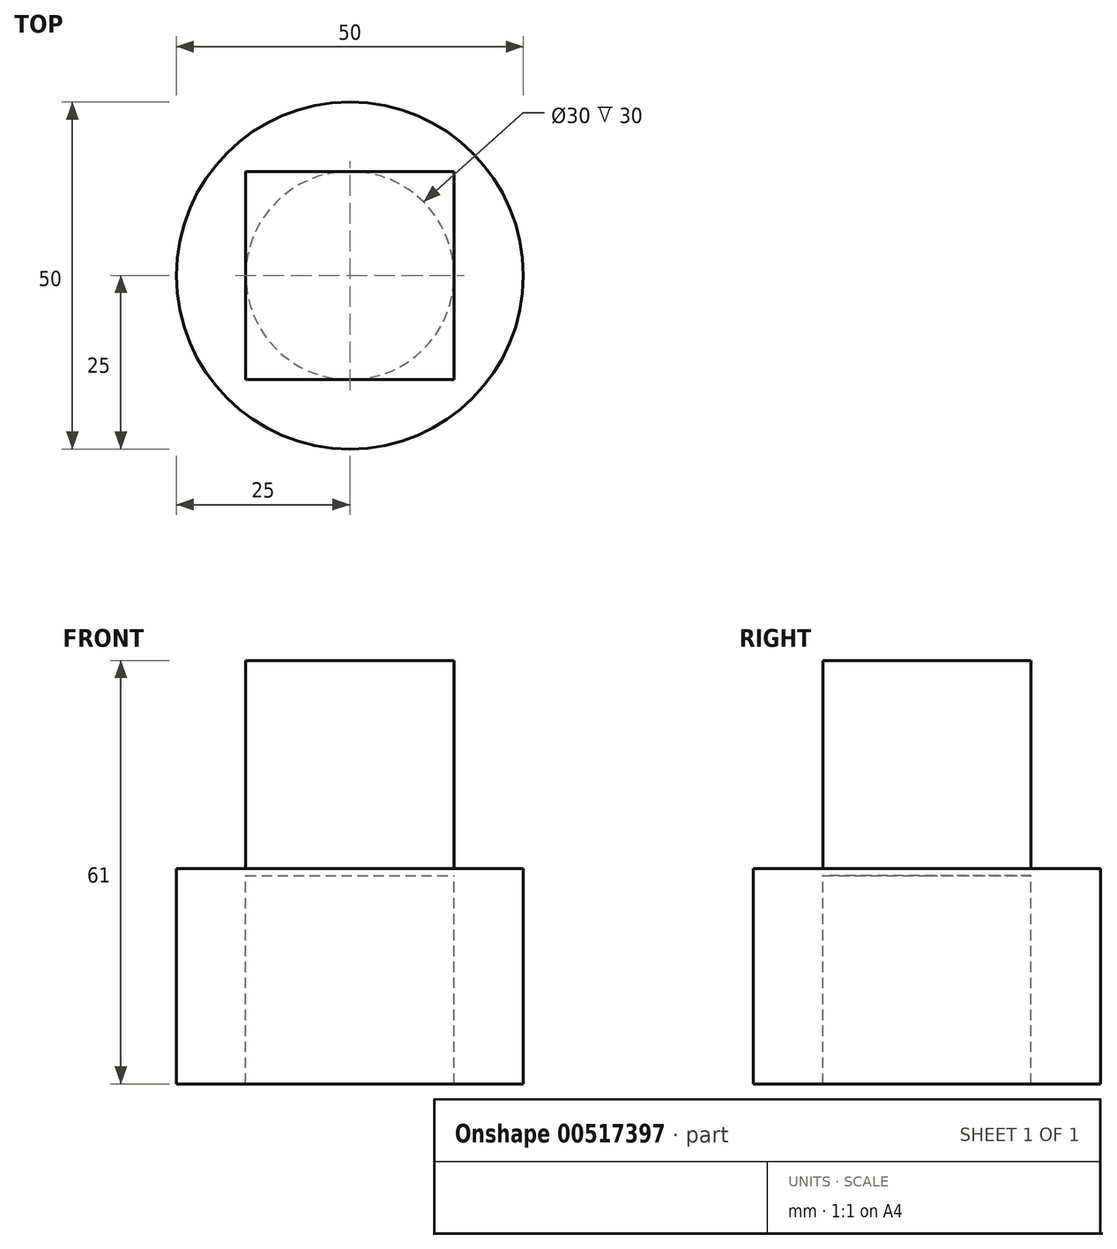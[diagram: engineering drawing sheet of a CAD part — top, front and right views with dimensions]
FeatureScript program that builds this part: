
annotation { "Feature Type Name" : "Feature", "Feature Type Description" : "" }
export const myFeature = defineFeature(function(context is Context, id is Id, definition is map)
    precondition{}
    {
        {
            var Q0;
            Q0=qCreatedBy(makeId("Top.planeOp"),FACE);
            var sketch = newSketch(context, id + "F0", { "sketchPlane" : qUnion([Q0])});
            skLineSegment(sketch, "E0.bottom", {"start": v(15, 15) * mm, "end": v(-15, 15) * mm});
            skLineSegment(sketch, "E0.top", {"start": v(15, -15) * mm, "end": v(-15, -15) * mm});
            skLineSegment(sketch, "E0.left", {"start": v(15, 15) * mm, "end": v(15, -15) * mm});
            skLineSegment(sketch, "E0.right", {"start": v(-15, 15) * mm, "end": v(-15, -15) * mm});
            skPoint(sketch, "E0.middle", {"position": v(0, 0) * mm});
            skSolve(sketch);
        }
        {
            var Q0;
            Q0=makeQuery(id+"F0.imprint","IMPRINT",FACE,{"disambiguationData":[TD([[makeQuery(id+"F0.imprint","IMPRINT",EDGE,{"derivedFrom":sQuery(id+"F0.wireOp",EDGE,"E0.bottom")}),1.0]])]});
            extrude(context, id + "F1", {"entities" : qUnion([Q0]), "depth" : 30 * mm, "offsetDistance" : 25 * mm});
        }
        {
            var Q0;
            Q0=makeQuery(id+"F1.opExtrude","CAP_FACE",FACE,{"disambiguationData":[OSD([sQuery(id+"F0.wireOp",EDGE,"E0.bottom"),sQuery(id+"F0.wireOp",EDGE,"E0.top"),sQuery(id+"F0.wireOp",EDGE,"E0.left"),sQuery(id+"F0.wireOp",EDGE,"E0.right")])],"isStart":true});
            var sketch = newSketch(context, id + "F2", { "sketchPlane" : qUnion([Q0])});
            skCircle(sketch, "E1", {"center": v(0, 0) * mm, "radius": 25 * mm});
            skCircle(sketch, "E2", {"center": v(0, 0) * mm, "radius": 15 * mm});
            skSolve(sketch);
        }
        {
            var Q0;
            Q0=makeQuery(id+"F2.imprint","IMPRINT",FACE,{"disambiguationData":[TD([[makeQuery(id+"F2.imprint","IMPRINT",EDGE,{"derivedFrom":sQuery(id+"F2.wireOp",EDGE,"E1")}),1.0]])]});
            var Q1;
            {var subQ0=sQuery(id+"F2.wireOp",EDGE,"E2");var subQ1=makeQuery(id+"F2.imprint","INTERSECT",VERTEX,{"derivedFrom":[makeQuery(id+"F1.opExtrude","CAP_EDGE",EDGE,{"disambiguationData":[OSD([sQuery(id+"F0.wireOp",EDGE,"E0.top")])],"isStart":true}),subQ0]});Q1=makeQuery(id+"F2.imprint","IMPRINT",FACE,{"disambiguationData":[TD([[makeQuery(id+"F2.imprint","IMPRINT",EDGE,{"disambiguationData":[TD([[subQ1,1.0]])],"derivedFrom":subQ0}),1.0]])]});}
            var Q2;
            {var subQ0=sQuery(id+"F2.wireOp",EDGE,"E2");var subQ1=makeQuery(id+"F1.opExtrude","CAP_EDGE",EDGE,{"disambiguationData":[OSD([sQuery(id+"F0.wireOp",EDGE,"E0.top")])],"isStart":true});var subQ2=makeQuery(id+"F2.imprint","INTERSECT",VERTEX,{"derivedFrom":[subQ1,subQ0]});Q2=makeQuery(id+"F2.imprint","IMPRINT",FACE,{"disambiguationData":[TD([[makeQuery(id+"F2.imprint","IMPRINT",EDGE,{"disambiguationData":[TD([[subQ2,-1.0]])],"derivedFrom":subQ0}),-1.0]])]});}
            var Q3;
            {var subQ0=sQuery(id+"F2.wireOp",EDGE,"E2");var subQ1=makeQuery(id+"F1.opExtrude","CAP_EDGE",EDGE,{"disambiguationData":[OSD([sQuery(id+"F0.wireOp",EDGE,"E0.top")])],"isStart":true});var subQ2=makeQuery(id+"F2.imprint","INTERSECT",VERTEX,{"derivedFrom":[subQ1,subQ0]});Q3=makeQuery(id+"F2.imprint","IMPRINT",FACE,{"disambiguationData":[TD([[makeQuery(id+"F2.imprint","IMPRINT",EDGE,{"disambiguationData":[TD([[subQ2,1.0]])],"derivedFrom":subQ0}),-1.0]])]});}
            var Q4;
            {var subQ0=sQuery(id+"F2.wireOp",EDGE,"E2");var subQ1=makeQuery(id+"F1.opExtrude","CAP_EDGE",EDGE,{"disambiguationData":[OSD([sQuery(id+"F0.wireOp",EDGE,"E0.left")])],"isStart":true});var subQ2=makeQuery(id+"F2.imprint","INTERSECT",VERTEX,{"derivedFrom":[subQ1,subQ0]});Q4=makeQuery(id+"F2.imprint","IMPRINT",FACE,{"disambiguationData":[TD([[makeQuery(id+"F2.imprint","IMPRINT",EDGE,{"disambiguationData":[TD([[subQ2,1.0]])],"derivedFrom":subQ0}),-1.0]])]});}
            var Q5;
            {var subQ0=sQuery(id+"F2.wireOp",EDGE,"E2");var subQ1=makeQuery(id+"F1.opExtrude","CAP_EDGE",EDGE,{"disambiguationData":[OSD([sQuery(id+"F0.wireOp",EDGE,"E0.right")])],"isStart":true});var subQ2=makeQuery(id+"F2.imprint","INTERSECT",VERTEX,{"derivedFrom":[subQ1,subQ0]});Q5=makeQuery(id+"F2.imprint","IMPRINT",FACE,{"disambiguationData":[TD([[makeQuery(id+"F2.imprint","IMPRINT",EDGE,{"disambiguationData":[TD([[subQ2,-1.0]])],"derivedFrom":subQ0}),-1.0]])]});}
            extrude(context, id + "F3", {"entities" : qUnion([Q0, Q1, Q2, Q3, Q4, Q5]), "operationType" : NewBodyOperationType.ADD, "depth" : 1 * mm, "offsetDistance" : 25 * mm});
        }
        {
            var Q0;
            Q0=makeQuery(id+"F3.opExtrude","CAP_FACE",FACE,{"disambiguationData":[OSD([sQuery(id+"F2.wireOp",EDGE,"E1")])],"isStart":false});
            var sketch = newSketch(context, id + "F4", { "sketchPlane" : qUnion([Q0])});
            skCircle(sketch, "E3.0", {"center": v(0, 0) * mm, "radius": 15 * mm});
            skCircle(sketch, "E4.0", {"center": v(0, 0) * mm, "radius": 25 * mm});
            skSolve(sketch);
        }
        {
            var Q0;
            Q0=makeQuery(id+"F4.imprint","IMPRINT",FACE,{"disambiguationData":[TD([[makeQuery(id+"F4.imprint","IMPRINT",EDGE,{"derivedFrom":sQuery(id+"F4.wireOp",EDGE,"E3.0")}),-1.0]])]});
            extrude(context, id + "F5", {"entities" : qUnion([Q0]), "operationType" : NewBodyOperationType.ADD, "depth" : 30 * mm, "offsetDistance" : 25 * mm});
        }
    });
